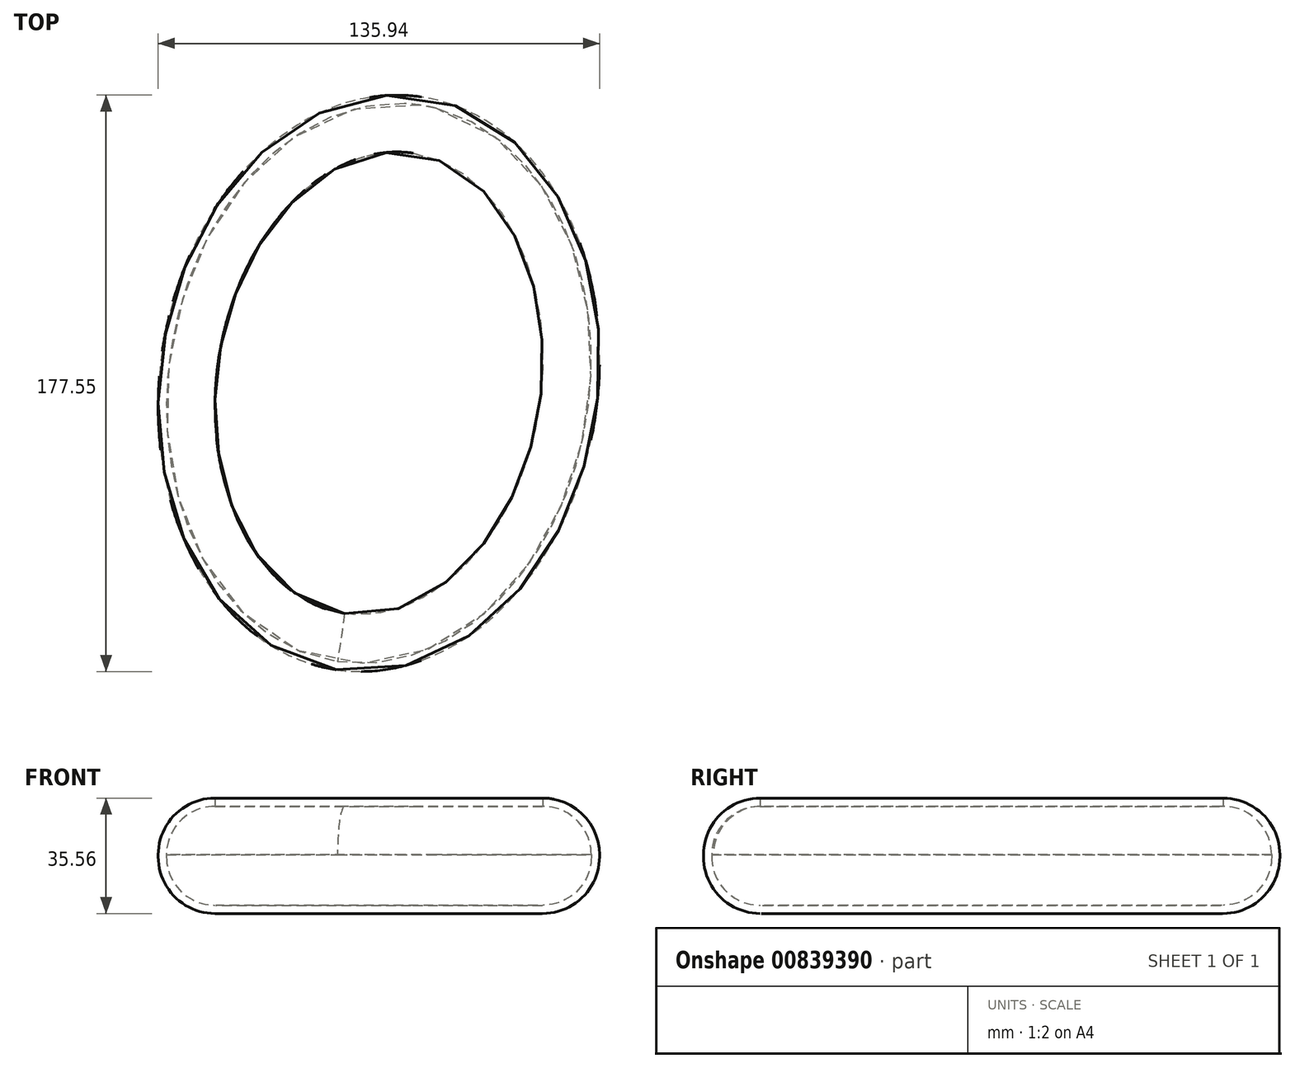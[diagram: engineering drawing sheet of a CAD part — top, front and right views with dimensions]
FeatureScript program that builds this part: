
annotation { "Feature Type Name" : "Feature", "Feature Type Description" : "" }
export const myFeature = defineFeature(function(context is Context, id is Id, definition is map)
    precondition{}
    {
        {
            var Q0;
            Q0=qCreatedBy(makeId("Top.planeOp"),FACE);
            var sketch = newSketch(context, id + "F0", { "sketchPlane" : qUnion([Q0])});
            skEllipse(sketch, "E0", {"center": v(-146.58, 29.63) * mm, "majorRadius": 89.19 * mm, "minorRadius": 67.43 * mm, "majorAxis": v(-0.15, -0.99)});
            skSolve(sketch);
        }
        {
            var Q0;
            Q0=makeQuery(id+"F0.imprint","IMPRINT",FACE,{"disambiguationData":[TD([[makeQuery(id+"F0.imprint","IMPRINT",EDGE,{"derivedFrom":sQuery(id+"F0.wireOp",EDGE,"E0")}),1.0]])]});
            extrude(context, id + "F1", {"entities" : qUnion([Q0]), "depth" : 35.56 * mm, "offsetDistance" : 25.4 * mm});
        }
        {
            var Q0;
            Q0=makeQuery(id+"F1.opExtrude","SWEPT_FACE",FACE,{"disambiguationData":[OSD([sQuery(id+"F0.wireOp",EDGE,"E0")])]});
            var Q1;
            Q1=makeQuery(id+"F1.opExtrude","CAP_FACE",FACE,{"disambiguationData":[OSD([sQuery(id+"F0.wireOp",EDGE,"E0")])],"isStart":false});
            fillet(context, id + "F2", {"entities" : qUnion([Q0, Q1]), "radius" : 17.5 * mm, "tangentPropagation" : true, "allowEdgeOverflow" : false});
        }
        {
            var Q0;
            Q0=makeQuery(id+"F1.opExtrude","CAP_FACE",FACE,{"disambiguationData":[OSD([sQuery(id+"F0.wireOp",EDGE,"E0")])],"isStart":false});
            shell(context, id + "F3", {"entities" : qUnion([Q0]), "thickness" : 2.54 * mm});
        }
    });
